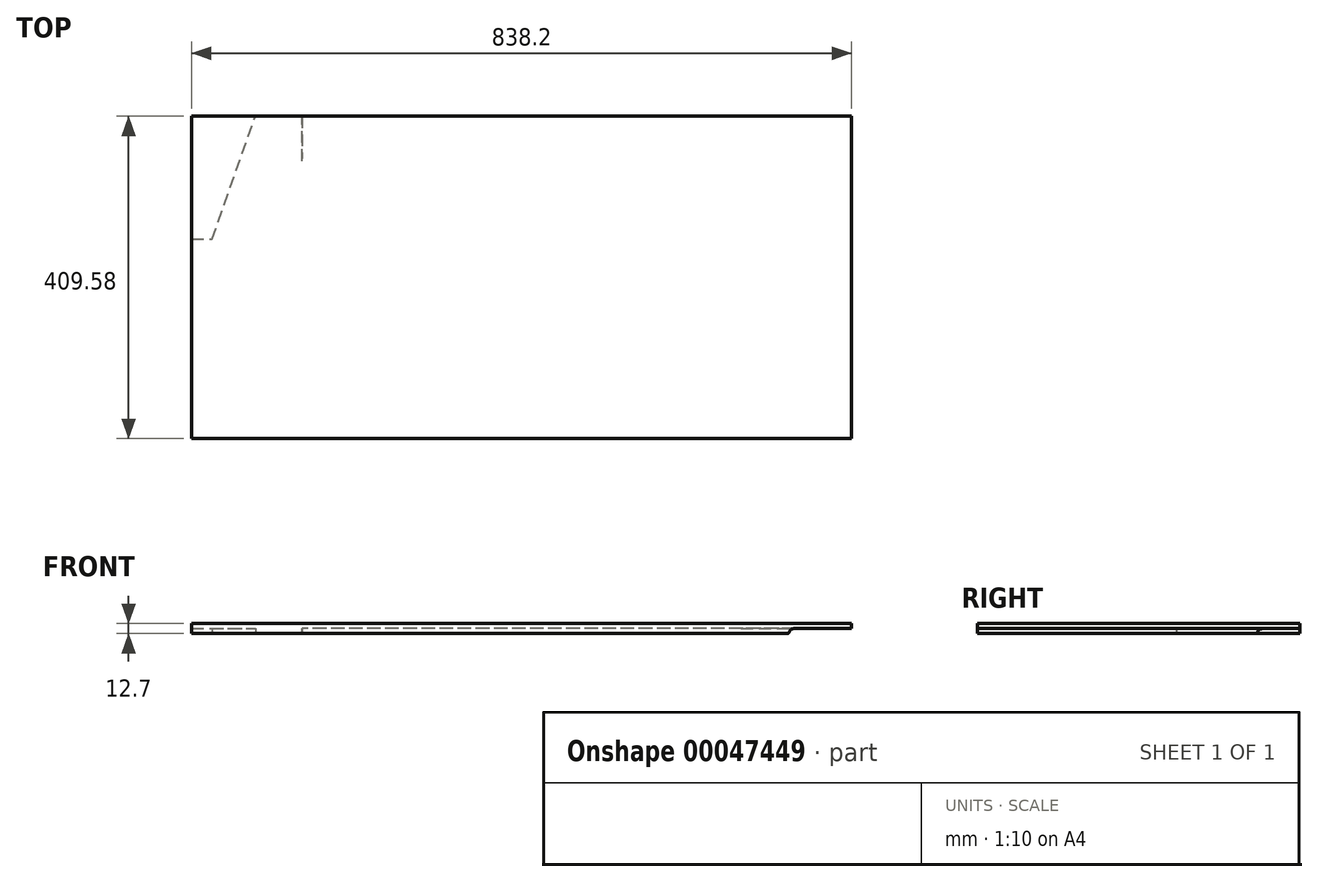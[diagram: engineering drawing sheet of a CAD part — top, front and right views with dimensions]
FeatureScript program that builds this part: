
annotation { "Feature Type Name" : "Feature", "Feature Type Description" : "" }
export const myFeature = defineFeature(function(context is Context, id is Id, definition is map)
    precondition{}
    {
        {
            var Q0;
            Q0=qCreatedBy(makeId("Top.planeOp"),FACE);
            var sketch = newSketch(context, id + "F0", { "sketchPlane" : qUnion([Q0])});
            skLineSegment(sketch, "E0.rect.bottom", {"start": v(419.1, 204.79) * mm, "end": v(-419.1, 204.79) * mm});
            skLineSegment(sketch, "E0.rect.top", {"start": v(419.1, -204.79) * mm, "end": v(-419.1, -204.79) * mm});
            skLineSegment(sketch, "E0.rect.left", {"start": v(419.1, 204.79) * mm, "end": v(419.1, -204.79) * mm});
            skLineSegment(sketch, "E0.rect.right", {"start": v(-419.1, 204.79) * mm, "end": v(-419.1, -204.79) * mm});
            skPoint(sketch, "E0.rect.middle", {"position": v(0, 0) * mm});
            skSolve(sketch);
        }
        {
            var Q0;
            Q0=makeQuery(id+"F0.imprint","IMPRINT",FACE,{"disambiguationData":[TD([[makeQuery(id+"F0.imprint","IMPRINT",EDGE,{"derivedFrom":sQuery(id+"F0.wireOp",EDGE,"E0.rect.bottom")}),1.0]])]});
            extrude(context, id + "F1", {"entities" : qUnion([Q0]), "depth" : 12.7 * mm});
        }
        {
            var Q0;
            Q0=makeQuery(id+"F1.opExtrude","CAP_FACE",FACE,{"disambiguationData":[OSD([sQuery(id+"F0.wireOp",EDGE,"E0.rect.bottom"),sQuery(id+"F0.wireOp",EDGE,"E0.rect.top"),sQuery(id+"F0.wireOp",EDGE,"E0.rect.left"),sQuery(id+"F0.wireOp",EDGE,"E0.rect.right")])],"isStart":true});
            var sketch = newSketch(context, id + "F2", { "sketchPlane" : qUnion([Q0])});
            skLineSegment(sketch, "E1", {"start": v(-339.73, 204.79) * mm, "end": v(-339.73, -89.85) * mm});
            skLineSegment(sketch, "E2", {"start": v(-278.77, -150.81) * mm, "end": v(278.77, -150.81) * mm});
            skLineSegment(sketch, "E3", {"start": v(339.73, -89.85) * mm, "end": v(339.73, 204.79) * mm});
            skPoint(sketch, "E4.visualSharp", {"position": v(-339.73, -150.81) * mm});
            skArc(sketch, "E4.filletArc", {"start": v(-339.73, -89.85) * mm, "mid": v(-321.87, -132.96) * mm, "end": v(-278.77, -150.81) * mm});
            skPoint(sketch, "E5.visualSharp", {"position": v(339.73, -150.81) * mm});
            skArc(sketch, "E5.filletArc", {"start": v(278.77, -150.81) * mm, "mid": v(321.87, -132.96) * mm, "end": v(339.73, -89.85) * mm});
            skSolve(sketch);
        }
        {
            var Q0;
            Q0=makeQuery(id+"F1.opExtrude","SWEPT_FACE",FACE,{"disambiguationData":[OSD([sQuery(id+"F0.wireOp",EDGE,"E0.rect.top")])]});
            var sketch = newSketch(context, id + "F3", { "sketchPlane" : qUnion([Q0])});
            skLineSegment(sketch, "E6", {"start": v(419.1, 6.35) * mm, "end": v(346.08, 6.35) * mm});
            skLineSegment(sketch, "E7", {"start": v(339.73, 0) * mm, "end": v(339.73, 0) * mm});
            skPoint(sketch, "E8.visualSharp", {"position": v(339.73, 6.35) * mm});
            skArc(sketch, "E8.filletArc", {"start": v(346.08, 6.35) * mm, "mid": v(342.4, 5.18) * mm, "end": v(340.09, 2.12) * mm});
            skLineSegment(sketch, "E9", {"start": v(337.1, 0) * mm, "end": v(334.1, 0) * mm});
            skLineSegment(sketch, "E10", {"start": v(334.1, 0) * mm, "end": v(334.1, -8.35) * mm});
            skLineSegment(sketch, "E11", {"start": v(334.1, -8.35) * mm, "end": v(419.1, -8.35) * mm});
            skLineSegment(sketch, "E12", {"start": v(419.1, -8.35) * mm, "end": v(419.1, 6.35) * mm});
            skPoint(sketch, "E13.visualSharp", {"position": v(339.73, 0) * mm});
            skArc(sketch, "E13.filletArc", {"start": v(337.1, 0) * mm, "mid": v(338.93, 0.58) * mm, "end": v(340.09, 2.12) * mm});
            skLineSegment(sketch, "E14", {"start": v(0, 12.7) * mm, "end": v(0, 0) * mm, "construction": true});
            skArc(sketch, "E15.MirrorCS", {"start": v(-337.1, 0) * mm, "mid": v(-338.93, 0.58) * mm, "end": v(-340.09, 2.12) * mm});
            skLineSegment(sketch, "E16.MirrorCS", {"start": v(-337.1, 0) * mm, "end": v(-334.1, 0) * mm});
            skArc(sketch, "E17.MirrorCS", {"start": v(-346.08, 6.35) * mm, "mid": v(-342.4, 5.18) * mm, "end": v(-340.09, 2.12) * mm});
            skPoint(sketch, "E18.MirrorP", {"position": v(-339.73, 0) * mm});
            skLineSegment(sketch, "E19.MirrorCS", {"start": v(-334.1, 0) * mm, "end": v(-334.1, -8.35) * mm});
            skLineSegment(sketch, "E20.MirrorCS", {"start": v(-339.73, 0) * mm, "end": v(-339.73, 0) * mm});
            skLineSegment(sketch, "E21.MirrorCS", {"start": v(-419.1, 6.35) * mm, "end": v(-346.08, 6.35) * mm});
            skPoint(sketch, "E22.MirrorP", {"position": v(-339.73, 6.35) * mm});
            skLineSegment(sketch, "E23.MirrorCS", {"start": v(-419.1, -8.35) * mm, "end": v(-419.1, 6.35) * mm});
            skLineSegment(sketch, "E24.MirrorCS", {"start": v(-334.1, -8.35) * mm, "end": v(-419.1, -8.35) * mm});
            skSolve(sketch);
        }
        {
            var Q0;
            {var subQ5=sQuery(id+"F3.wireOp",EDGE,"E6");Q0=makeQuery(id+"F3.imprint","IMPRINT",FACE,{"disambiguationData":[TD([[makeQuery(id+"F3.imprint","IMPRINT",EDGE,{"derivedFrom":subQ5}),1.0]])]});}
            var Q1;
            {var subQ1=sQuery(id+"F3.wireOp",EDGE,"E9");Q1=makeQuery(id+"F3.imprint","IMPRINT",FACE,{"disambiguationData":[TD([[makeQuery(id+"F3.imprint","IMPRINT",EDGE,{"derivedFrom":subQ1}),1.0]])]});}
            var Q2;
            Q2=sQuery(id+"F2.wireOp",EDGE,"E3");
            var Q3;
            Q3=sQuery(id+"F2.wireOp",EDGE,"E5.filletArc");
            var Q4;
            Q4=sQuery(id+"F2.wireOp",EDGE,"E2");
            sweep(context, id + "F4", {"operationType" : NewBodyOperationType.REMOVE, "profiles" : qUnion([Q0, Q1]), "path" : qUnion([Q2, Q3, Q4])});
        }
        {
            var Q0;
            {var subQ0=sQuery(id+"F3.wireOp",EDGE,"E16.MirrorCS");Q0=makeQuery(id+"F3.imprint","IMPRINT",FACE,{"disambiguationData":[TD([[makeQuery(id+"F3.imprint","IMPRINT",EDGE,{"derivedFrom":subQ0}),1.0]])]});}
            var Q1;
            {var subQ0=sQuery(id+"F3.wireOp",EDGE,"E15.MirrorCS");Q1=makeQuery(id+"F3.imprint","IMPRINT",FACE,{"disambiguationData":[TD([[makeQuery(id+"F3.imprint","IMPRINT",EDGE,{"derivedFrom":subQ0}),1.0]])]});}
            var Q2;
            Q2=sQuery(id+"F2.wireOp",EDGE,"E1");
            var Q3;
            Q3=sQuery(id+"F2.wireOp",EDGE,"E4.filletArc");
            sweep(context, id + "F5", {"operationType" : NewBodyOperationType.REMOVE, "profiles" : qUnion([Q0, Q1]), "path" : qUnion([Q2, Q3])});
        }
        {
            var Q0;
            {var subQ4=sQuery(id+"F2.wireOp",EDGE,"E1");Q0=makeQuery(id+"F2.imprint","IMPRINT",FACE,{"disambiguationData":[TD([[makeQuery(id+"F2.imprint","IMPRINT",EDGE,{"derivedFrom":subQ4}),-1.0]])]});}
            var sketch = newSketch(context, id + "F6", { "sketchPlane" : qUnion([Q0])});
            skLineSegment(sketch, "E25", {"start": v(-452.75, -48.87) * mm, "end": v(-393.23, -48.87) * mm});
            skLineSegment(sketch, "E26", {"start": v(-393.23, -48.87) * mm, "end": v(-328.93, -230.15) * mm});
            skLineSegment(sketch, "E27", {"start": v(-328.93, -230.15) * mm, "end": v(-471.22, -238.36) * mm});
            skLineSegment(sketch, "E28", {"start": v(-471.22, -238.36) * mm, "end": v(-452.75, -48.87) * mm});
            skLineSegment(sketch, "E29", {"start": v(311.36, -234.26) * mm, "end": v(437.92, 9.27) * mm});
            skLineSegment(sketch, "E30", {"start": v(437.92, 9.27) * mm, "end": v(450.23, -257.51) * mm});
            skLineSegment(sketch, "E31", {"start": v(450.23, -257.51) * mm, "end": v(311.36, -234.26) * mm});
            skSolve(sketch);
        }
        {
            var Q0;
            Q0 = qSketchRegion(id + "F6", true);
            extrude(context, id + "F7", {"entities" : qUnion([Q0]), "operationType" : NewBodyOperationType.REMOVE, "oppositeDirection" : true, "depth" : 6.35 * mm});
        }
    });
